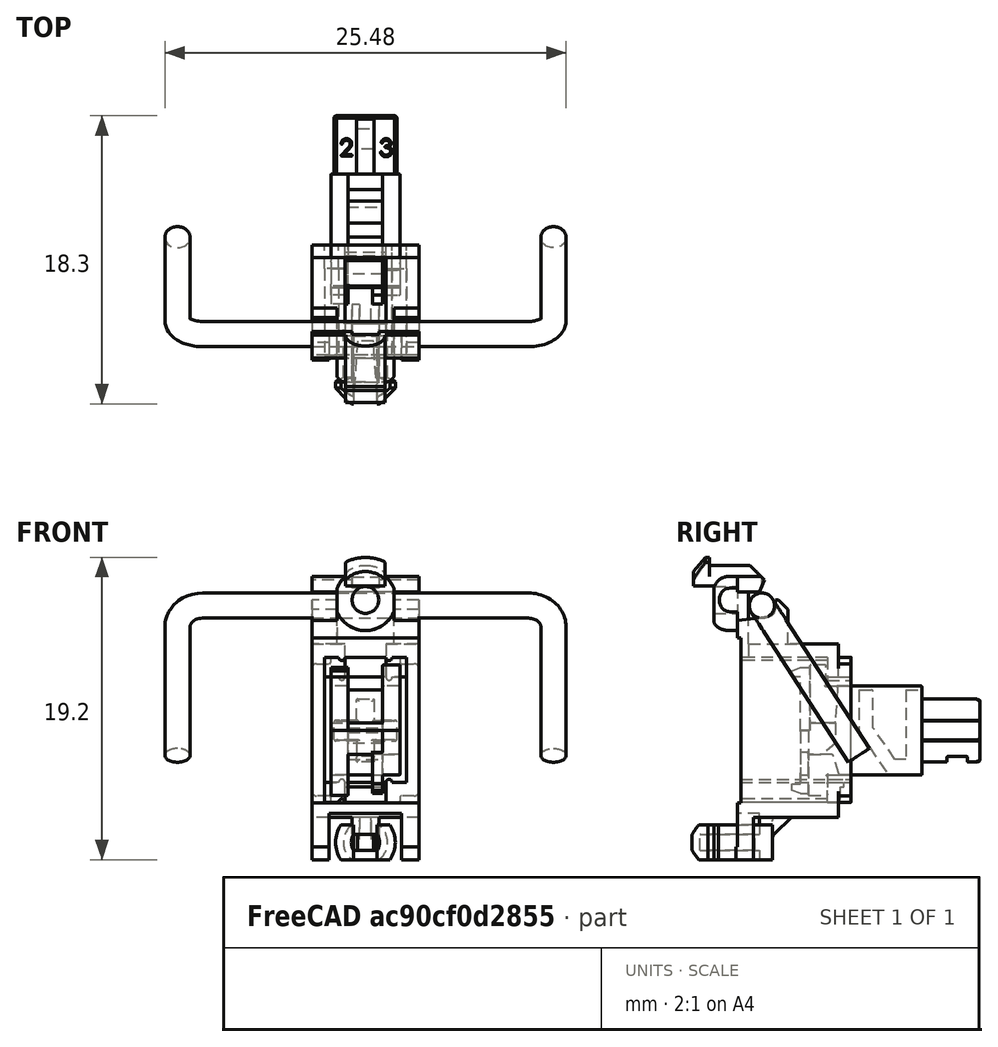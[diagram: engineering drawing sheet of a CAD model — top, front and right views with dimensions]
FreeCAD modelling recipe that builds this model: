
FCSTD DOCUMENT  (FreeCAD 0.18R16158 (Git))
Label: Stabilizer_Cherry_MX_2u
License: CreativeCommons Attribution-ShareAlike
LicenseURL: http://creativecommons.org/licenses/by-sa/4.0/
objects: Part::Feature×4, App::Part×3, PartDesign::Plane×2, Sketcher::SketchObject×2, PartDesign::AdditivePipe×1, PartDesign::Body×1
note: 11 computed .brp shape members not serialized (recipe doc carries the construction recipe); baked Part::Feature solids carry a one-line shape summary decoded from their .brp

FEATURE [Part::Feature] Part__Feature  label="Stabilizer_Base"
  shape: bbox 6.802 x 10.1 x 19.67 mm, 163 faces (baked)
FEATURE [Part::Feature] Part__Feature001  label="Stabilizer_Key"
  Placement = pos=(0,8.1,0) rot=(0,0,1;0rad)
  shape: bbox 4.6 x 11.96 x 8.302 mm, 299 faces (baked)
FEATURE [App::Part] Part  label="Stabilizer_End_1"
  Group = -> [Part__Feature001,Part__Feature]
  Origin = -> Origin001
  Placement = pos=(-11.94,0,0) rot=(0,0,1;0rad)
FEATURE [PartDesign::Plane] DatumPlane
  Length = 42.0556
  MapMode = 13
  Placement = pos=(23.0333,0.289849,4.3056) rot=(1,0,0;2.14498rad)
  ResizeMode = 0
  Width = 33.9458
FEATURE [PartDesign::Plane] DatumPlane001
  Length = 32.9636
  MapMode = 11
  Placement = pos=(8e-15,4.09188,-1.57187) rot=(0.272451,-0.272451,0.92279;1.65106rad)
  ResizeMode = 0
  Width = 30.7762
FEATURE [Sketcher::SketchObject] Sketch
  MapMode = 5
  Placement = pos=(8e-15,4.09188,-1.57187) rot=(0.272451,-0.272451,0.92279;1.65106rad)
  Support = -> [DatumPlane001]
  sketch-geometry (5):
    g0: Circle CenterX=0 CenterY=11.938 CenterZ=0 NormalX=0 NormalY=0 NormalZ=1 AngleXU=0 Radius=0.8
    g1: Circle [constr] CenterX=0 CenterY=-11.938 CenterZ=0 NormalX=0 NormalY=0 NormalZ=1 AngleXU=0 Radius=0.8
    g2: LineSegment [constr] StartX=0 StartY=11.938 StartZ=0 EndX=0 EndY=0 EndZ=0
    g3: LineSegment [constr] StartX=0 StartY=0 StartZ=0 EndX=0 EndY=-11.938 EndZ=0
    g4: GeomPoint X=0 Y=-11.938 Z=0
  constraints (11):
    c: Diameter(g0) = 1.6
    c: PointOnObject(g0,g-2)
    c: PointOnObject(g1,g-2)
    c: Coincident(g2,g0)
    c: Coincident(g2,g-1)
    c: Coincident(g3,g-1)
    c: Coincident(g3,g1)
    c: Equal(g3,g2)
    c: Distance(g2) = 11.938
    c: Equal(g1,g0)
    c: Coincident(g4,g1)
FEATURE [Sketcher::SketchObject] Sketch001
  ExternalGeometry = -> [Sketch]
  MapMode = 5
  Placement = pos=(23.0333,0.289849,4.3056) rot=(1,0,0;2.14498rad)
  Support = -> [DatumPlane]
  sketch-geometry (5):
    g0: LineSegment StartX=-34.1713 StartY=-7 StartZ=0 EndX=-34.1713 EndY=2.73 EndZ=0
    g1: LineSegment StartX=-33.3713 StartY=3.53 StartZ=0 EndX=-12.6913 EndY=3.53 EndZ=0
    g2: LineSegment StartX=-11.8913 StartY=2.73 StartZ=0 EndX=-11.8913 EndY=-7 EndZ=0
    g3: ArcOfCircle CenterX=-33.3713 CenterY=2.73 CenterZ=0 NormalX=0 NormalY=0 NormalZ=1 AngleXU=0 Radius=0.8 StartAngle=1.5708 EndAngle=3.14159
    g4: ArcOfCircle CenterX=-12.6913 CenterY=2.73 CenterZ=0 NormalX=0 NormalY=0 NormalZ=1 AngleXU=0 Radius=0.8 StartAngle=0 EndAngle=1.5708
FEATURE [PartDesign::AdditivePipe] AdditivePipe
  AuxilleryCurvelinear = true
  AuxillerySpineTangent = false
  Binormal = (0,0,0)
  Mode = 0
  Placement = pos=(8e-15,4.09188,-1.57187) rot=(0.272451,-0.272451,0.92279;1.65106rad)
  Profile = -> Sketch
  Spine = -> Sketch001
  SpineTangent = false
  Transformation = 0
  Transition = 0
FEATURE [PartDesign::Body] Body  label="Bar"
  Group = -> [DatumPlane,DatumPlane001,Sketch,Sketch001,AdditivePipe]
  Origin = -> Origin002
  Tip = -> AdditivePipe
FEATURE [Part::Feature] Part__Feature002  label="Stabilizer_Key_"
  Placement = pos=(0,8.1,0) rot=(0,0,1;0rad)
  shape: bbox 4.6 x 11.96 x 8.302 mm, 299 faces (baked)
FEATURE [Part::Feature] Part__Feature003  label="Stabilizer_Base_"
  shape: bbox 6.802 x 10.1 x 19.67 mm, 163 faces (baked)
FEATURE [App::Part] Part001  label="Stabilizer_End_2"
  Group = -> [Part__Feature002,Part__Feature003]
  Origin = -> Origin003
  Placement = pos=(11.94,0,0) rot=(0,0,1;0rad)
FEATURE [App::Part] Stabilizer___open  label="Stabilizer_Cherry_MX_2u"
  Group = -> [Body,Part001,Part]
  Origin = -> Origin
  Placement = pos=(0,8e-16,3.65) rot=(1,0,0;1.5708rad)
